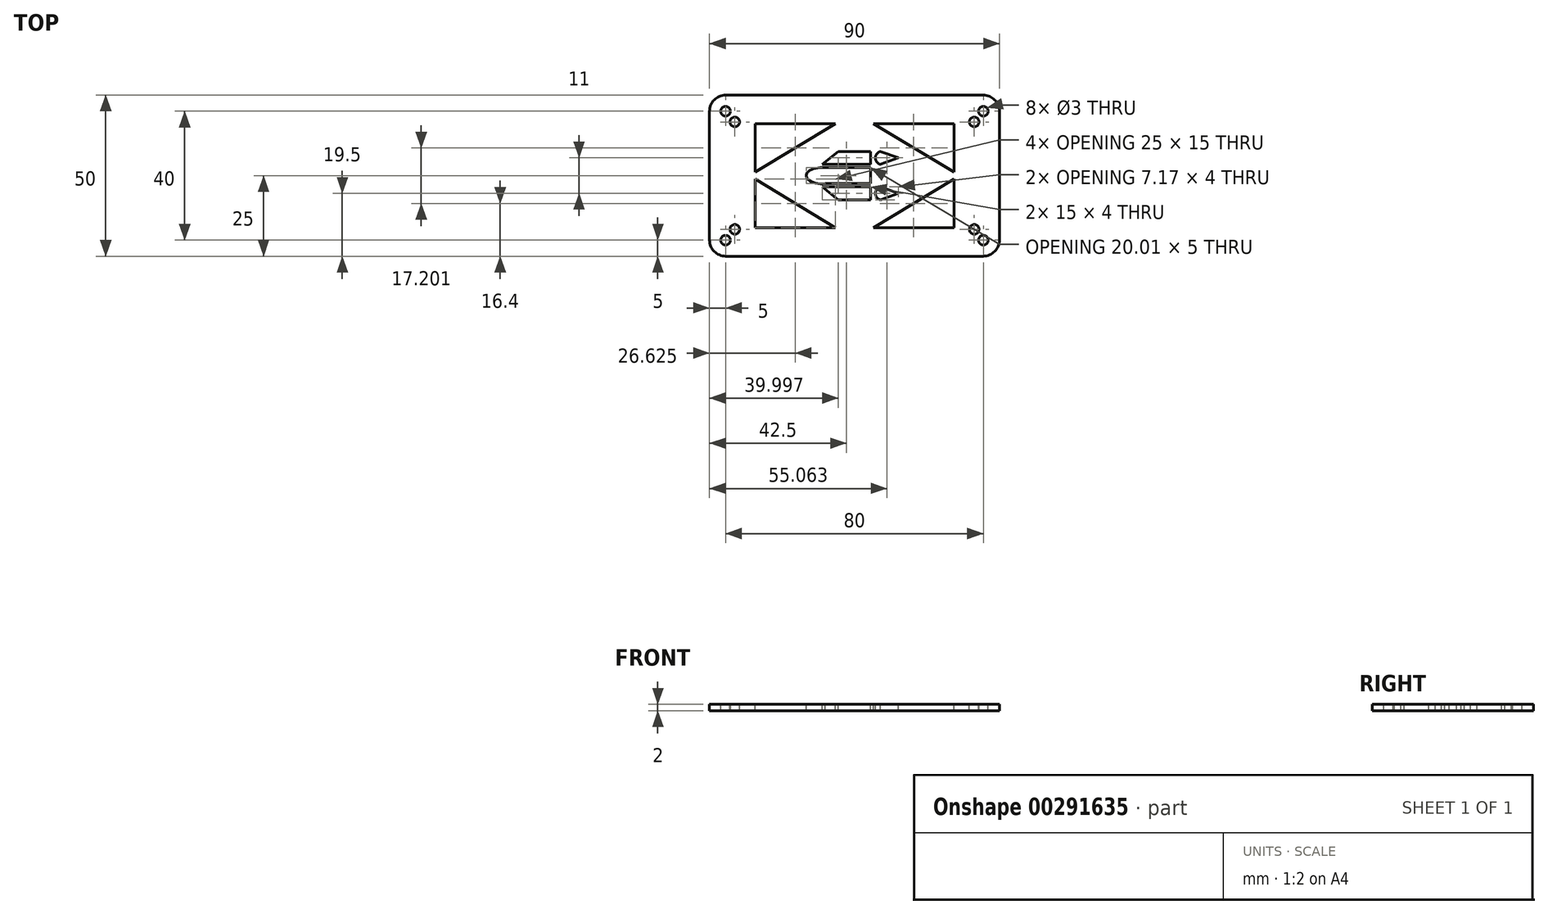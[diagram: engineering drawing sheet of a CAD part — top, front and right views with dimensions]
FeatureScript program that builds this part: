
annotation { "Feature Type Name" : "Feature", "Feature Type Description" : "" }
export const myFeature = defineFeature(function(context is Context, id is Id, definition is map)
    precondition{}
    {
        {
            var Q0;
            Q0=qCreatedBy(makeId("Top.planeOp"),FACE);
            var sketch = newSketch(context, id + "F0", { "sketchPlane" : qUnion([Q0])});
            skLineSegment(sketch, "E0.bottom", {"start": v(0, 0) * mm, "end": v(90, 0) * mm});
            skLineSegment(sketch, "E0.top", {"start": v(0, 50) * mm, "end": v(90, 50) * mm});
            skLineSegment(sketch, "E0.left", {"start": v(0, 0) * mm, "end": v(0, 50) * mm});
            skLineSegment(sketch, "E0.right", {"start": v(90, 0) * mm, "end": v(90, 50) * mm});
            skSolve(sketch);
        }
        {
            var Q0;
            Q0 = qSketchRegion(id + "F0", true);
            extrude(context, id + "F1", {"entities" : qUnion([Q0]), "depth" : 2 * mm});
        }
        {
            var Q0;
            Q0=makeQuery(id+"F1.opExtrude","CAP_FACE",FACE,{"disambiguationData":[OSD([sQuery(id+"F0.wireOp",EDGE,"E0.bottom"),sQuery(id+"F0.wireOp",EDGE,"E0.top"),sQuery(id+"F0.wireOp",EDGE,"E0.left"),sQuery(id+"F0.wireOp",EDGE,"E0.right")])],"isStart":false});
            cPlane(context, id + "F2", {"entities" : qUnion([Q0]), "cplaneType" : CPlaneType.OFFSET, "offset" : 0 * mm, "width" : 152.4 * mm, "height" : 152.4 * mm});
        }
        {
            var Q0;
            Q0=makeQuery(id+"F1.opExtrude","SWEPT_EDGE",EDGE,{"disambiguationData":[OSD([sQuery(id+"F0.wireOp",EDGE,"E0.bottom"),sQuery(id+"F0.wireOp",EDGE,"E0.right")])]});
            fillet(context, id + "F3", {"entities" : qUnion([Q0]), "radius" : 5.08 * mm, "tangentPropagation" : true, "allowEdgeOverflow" : false});
        }
        {
            var Q0;
            Q0=makeQuery(id+"F1.opExtrude","SWEPT_EDGE",EDGE,{"disambiguationData":[OSD([sQuery(id+"F0.wireOp",EDGE,"E0.top"),sQuery(id+"F0.wireOp",EDGE,"E0.right")])]});
            fillet(context, id + "F4", {"entities" : qUnion([Q0]), "radius" : 5.08 * mm, "tangentPropagation" : true, "allowEdgeOverflow" : false});
        }
        {
            var Q0;
            Q0=makeQuery(id+"F1.opExtrude","SWEPT_EDGE",EDGE,{"disambiguationData":[OSD([sQuery(id+"F0.wireOp",EDGE,"E0.top"),sQuery(id+"F0.wireOp",EDGE,"E0.left")])]});
            fillet(context, id + "F5", {"entities" : qUnion([Q0]), "radius" : 5.08 * mm, "tangentPropagation" : true, "allowEdgeOverflow" : false});
        }
        {
            var Q0;
            Q0=makeQuery(id+"F1.opExtrude","SWEPT_EDGE",EDGE,{"disambiguationData":[OSD([sQuery(id+"F0.wireOp",EDGE,"E0.bottom"),sQuery(id+"F0.wireOp",EDGE,"E0.left")])]});
            fillet(context, id + "F6", {"entities" : qUnion([Q0]), "radius" : 5.08 * mm, "tangentPropagation" : true, "allowEdgeOverflow" : false});
        }
        {
            var Q0;
            Q0=qCreatedBy(id+"F2.planeOp",FACE);
            var sketch = newSketch(context, id + "F7", { "sketchPlane" : qUnion([Q0])});
            skLineSegment(sketch, "E1", {"start": v(45, 0) * mm, "end": v(45, 70.78) * mm});
            skLineSegment(sketch, "E2", {"start": v(0, 25) * mm, "end": v(105.16, 25) * mm});
            skSolve(sketch);
        }
        {
            var Q0;
            Q0=qCreatedBy(id+"F2.planeOp",FACE);
            var sketch = newSketch(context, id + "F8", { "sketchPlane" : qUnion([Q0])});
            skCircle(sketch, "E3", {"center": v(85, 5) * mm, "radius": 1.5 * mm});
            skCircle(sketch, "E4", {"center": v(82.15, 8.34) * mm, "radius": 1.5 * mm});
            skCircle(sketch, "E5.MirrorC", {"center": v(82.15, 41.66) * mm, "radius": 1.5 * mm});
            skCircle(sketch, "E6.MirrorC", {"center": v(85, 45) * mm, "radius": 1.5 * mm});
            skCircle(sketch, "E7.MirrorC", {"center": v(7.85, 41.66) * mm, "radius": 1.5 * mm});
            skCircle(sketch, "E8.MirrorC", {"center": v(5, 45) * mm, "radius": 1.5 * mm});
            skCircle(sketch, "E9.MirrorC", {"center": v(7.85, 8.34) * mm, "radius": 1.5 * mm});
            skCircle(sketch, "E10.MirrorC", {"center": v(5, 5) * mm, "radius": 1.5 * mm});
            skSolve(sketch);
        }
        {
            var Q0;
            Q0 = qSketchRegion(id + "F8", true);
            extrude(context, id + "F9", {"entities" : qUnion([Q0]), "operationType" : NewBodyOperationType.REMOVE, "oppositeDirection" : true, "depth" : 25.4 * mm});
        }
        {
            var Q0;
            Q0=qCreatedBy(id+"F2.planeOp",FACE);
            var sketch = newSketch(context, id + "F10", { "sketchPlane" : qUnion([Q0])});
            skLineSegment(sketch, "E11.bottom", {"start": v(35, 27.5) * mm, "end": v(50, 27.5) * mm});
            skLineSegment(sketch, "E11.top", {"start": v(35, 22.5) * mm, "end": v(50, 22.5) * mm});
            skLineSegment(sketch, "E11.left", {"start": v(35, 27.5) * mm, "end": v(35, 22.5) * mm});
            skLineSegment(sketch, "E11.right", {"start": v(50, 27.5) * mm, "end": v(50, 22.5) * mm});
            skEllipse(sketch, "E12", {"center": v(35, 25) * mm, "majorRadius": 5 * mm, "minorRadius": 2.54 * mm, "majorAxis": v(-1, 0)});
            skLineSegment(sketch, "E13.bottom", {"start": v(40, 32.5) * mm, "end": v(50, 32.5) * mm});
            skLineSegment(sketch, "E13.top", {"start": v(40, 28.5) * mm, "end": v(50, 28.5) * mm});
            skLineSegment(sketch, "E13.left", {"start": v(40, 32.5) * mm, "end": v(40, 28.5) * mm});
            skLineSegment(sketch, "E13.right", {"start": v(50, 32.5) * mm, "end": v(50, 28.5) * mm});
            skLineSegment(sketch, "E14", {"start": v(40, 32.5) * mm, "end": v(35, 28.5) * mm});
            skLineSegment(sketch, "E15", {"start": v(35, 28.5) * mm, "end": v(40, 28.5) * mm});
            skLineSegment(sketch, "E16.MirrorCS", {"start": v(40, 17.5) * mm, "end": v(35, 21.5) * mm});
            skLineSegment(sketch, "E17.MirrorCS", {"start": v(35, 21.5) * mm, "end": v(40, 21.5) * mm});
            skLineSegment(sketch, "E18.MirrorCS", {"start": v(40, 17.5) * mm, "end": v(40, 21.5) * mm});
            skLineSegment(sketch, "E19.MirrorCS", {"start": v(40, 21.5) * mm, "end": v(50, 21.5) * mm});
            skLineSegment(sketch, "E20.MirrorCS", {"start": v(40, 17.5) * mm, "end": v(50, 17.5) * mm});
            skLineSegment(sketch, "E21.MirrorCS", {"start": v(50, 17.5) * mm, "end": v(50, 21.5) * mm});
            skArc(sketch, "E22", {"start": v(53, 32.5) * mm, "mid": v(51.48, 30.5) * mm, "end": v(53, 28.5) * mm});
            skArc(sketch, "E23.MirrorCS", {"start": v(53, 17.5) * mm, "mid": v(51.48, 19.5) * mm, "end": v(53, 21.5) * mm});
            skLineSegment(sketch, "E24", {"start": v(53, 32.5) * mm, "end": v(58.65, 30.5) * mm});
            skLineSegment(sketch, "E25", {"start": v(58.65, 30.5) * mm, "end": v(53, 28.5) * mm});
            skLineSegment(sketch, "E26.MirrorCS", {"start": v(58.65, 19.5) * mm, "end": v(53, 21.5) * mm});
            skLineSegment(sketch, "E27.MirrorCS", {"start": v(53, 17.5) * mm, "end": v(58.65, 19.5) * mm});
            skSolve(sketch);
        }
        {
            var Q0;
            Q0 = qSketchRegion(id + "F10", true);
            extrude(context, id + "F11", {"entities" : qUnion([Q0]), "operationType" : NewBodyOperationType.REMOVE, "oppositeDirection" : true, "depth" : 25.4 * mm});
        }
        {
            var Q0;
            Q0=qCreatedBy(id+"F2.planeOp",FACE);
            var sketch = newSketch(context, id + "F12", { "sketchPlane" : qUnion([Q0])});
            skLineSegment(sketch, "E28", {"start": v(50.87, 8.9) * mm, "end": v(75.87, 8.9) * mm});
            skLineSegment(sketch, "E29", {"start": v(75.87, 8.9) * mm, "end": v(75.87, 23.9) * mm});
            skLineSegment(sketch, "E30", {"start": v(75.87, 23.9) * mm, "end": v(50.87, 8.9) * mm});
            skLineSegment(sketch, "E31.MirrorCS", {"start": v(75.87, 26.1) * mm, "end": v(50.87, 41.1) * mm});
            skLineSegment(sketch, "E32.MirrorCS", {"start": v(50.87, 41.1) * mm, "end": v(75.87, 41.1) * mm});
            skLineSegment(sketch, "E33.MirrorCS", {"start": v(75.87, 41.1) * mm, "end": v(75.87, 26.1) * mm});
            skLineSegment(sketch, "E34.MirrorCS", {"start": v(39.13, 41.1) * mm, "end": v(14.13, 41.1) * mm});
            skLineSegment(sketch, "E35.MirrorCS", {"start": v(14.13, 26.1) * mm, "end": v(39.13, 41.1) * mm});
            skLineSegment(sketch, "E36.MirrorCS", {"start": v(14.13, 41.1) * mm, "end": v(14.13, 26.1) * mm});
            skLineSegment(sketch, "E37.MirrorCS", {"start": v(14.13, 23.9) * mm, "end": v(39.13, 8.9) * mm});
            skLineSegment(sketch, "E38.MirrorCS", {"start": v(14.13, 8.9) * mm, "end": v(14.13, 23.9) * mm});
            skLineSegment(sketch, "E39.MirrorCS", {"start": v(39.13, 8.9) * mm, "end": v(14.13, 8.9) * mm});
            skSolve(sketch);
        }
        {
            var Q0;
            Q0 = qSketchRegion(id + "F12", true);
            extrude(context, id + "F13", {"entities" : qUnion([Q0]), "operationType" : NewBodyOperationType.REMOVE, "oppositeDirection" : true, "depth" : 25.4 * mm});
        }
    });
